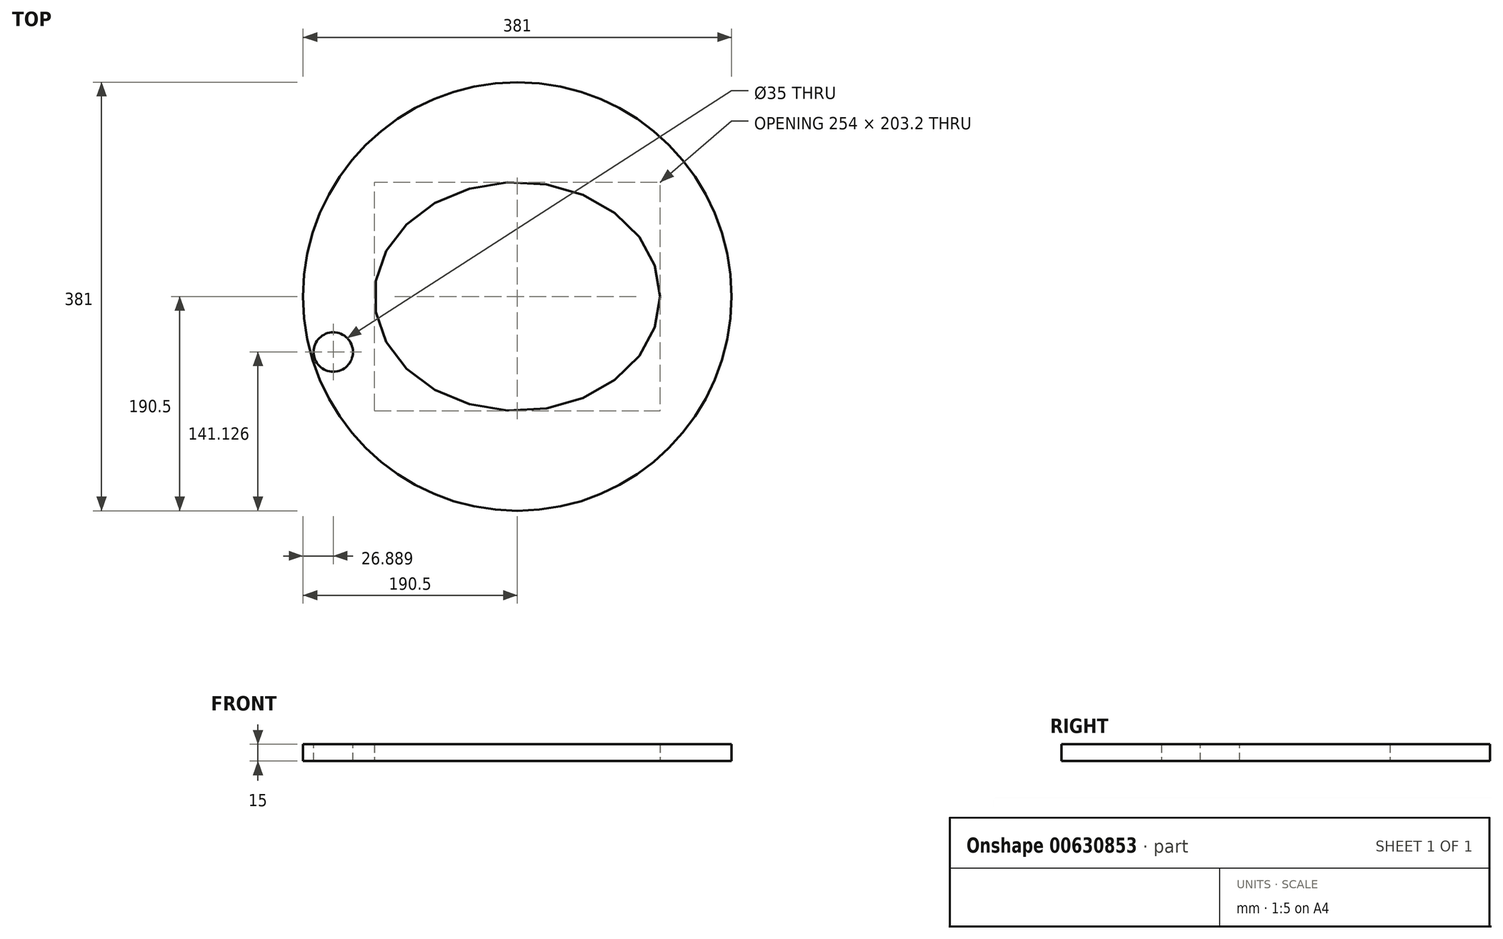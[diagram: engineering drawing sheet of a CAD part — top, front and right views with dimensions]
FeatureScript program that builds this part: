
annotation { "Feature Type Name" : "Feature", "Feature Type Description" : "" }
export const myFeature = defineFeature(function(context is Context, id is Id, definition is map)
    precondition{}
    {
        {
            var Q0;
            Q0=qCreatedBy(makeId("Top.planeOp"),FACE);
            var sketch = newSketch(context, id + "F0", { "sketchPlane" : qUnion([Q0])});
            skCircle(sketch, "E0", {"center": v(0, 0) * mm, "radius": 190.5 * mm});
            skEllipse(sketch, "E1", {"center": v(0, 0) * mm, "majorRadius": 127 * mm, "minorRadius": 101.6 * mm, "majorAxis": v(1, 0)});
            skSolve(sketch);
        }
        {
            var Q0;
            Q0=makeQuery(id+"F0.imprint","IMPRINT",FACE,{"disambiguationData":[TD([[makeQuery(id+"F0.imprint","IMPRINT",EDGE,{"derivedFrom":sQuery(id+"F0.wireOp",EDGE,"E0")}),1.0]])]});
            extrude(context, id + "F1", {"entities" : qUnion([Q0]), "depth" : 15 * mm, "offsetDistance" : 25.4 * mm});
        }
        {
            var Q0;
            Q0=makeQuery(id+"F1.opExtrude","CAP_FACE",FACE,{"disambiguationData":[OSD([sQuery(id+"F0.wireOp",EDGE,"E0"),sQuery(id+"F0.wireOp",EDGE,"E1")])],"isStart":false});
            var sketch = newSketch(context, id + "F2", { "sketchPlane" : qUnion([Q0])});
            skCircle(sketch, "E2", {"center": v(-163.61, -49.37) * mm, "radius": 17.5 * mm});
            skSolve(sketch);
        }
        {
            var Q0;
            Q0 = qSketchRegion(id + "F2", true);
            extrude(context, id + "F3", {"entities" : qUnion([Q0]), "operationType" : NewBodyOperationType.REMOVE, "oppositeDirection" : true, "depth" : 53.62 * mm, "offsetDistance" : 25.4 * mm});
        }
    });
